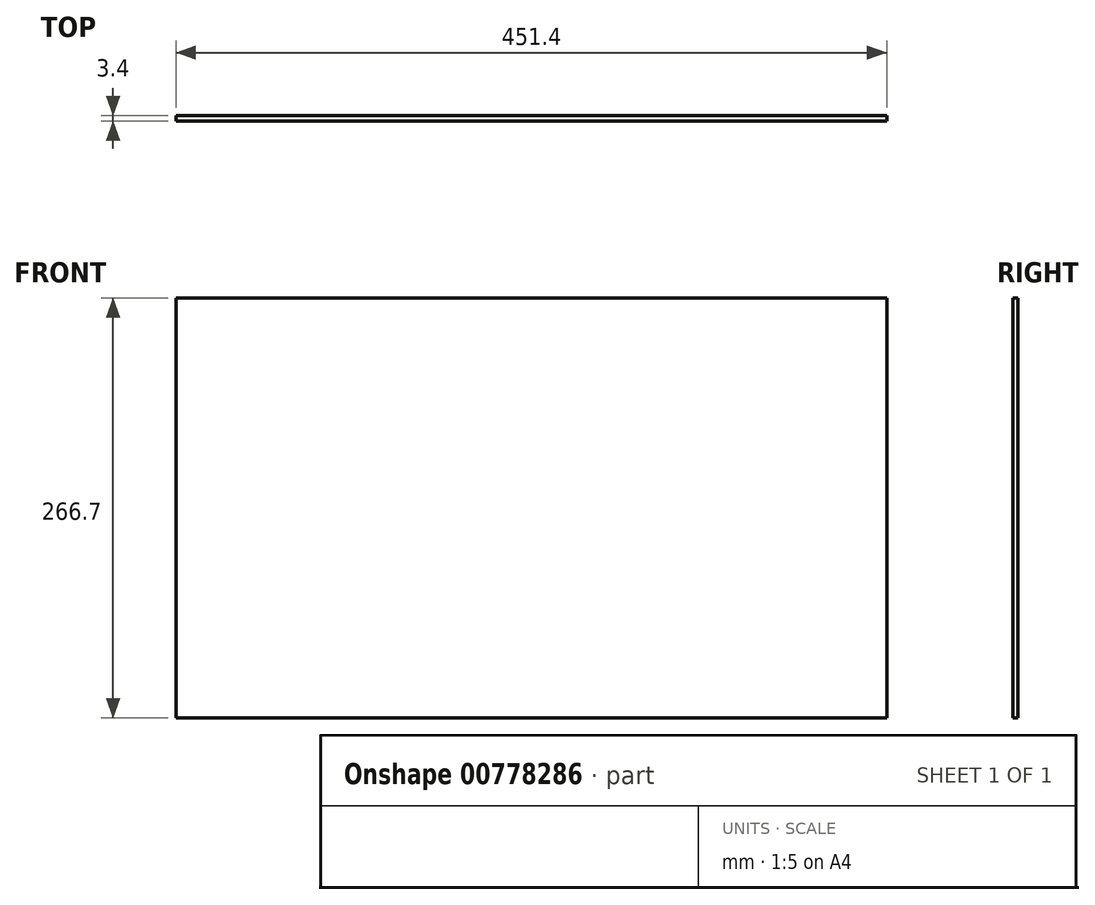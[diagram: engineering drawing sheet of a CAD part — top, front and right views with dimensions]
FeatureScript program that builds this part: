
annotation { "Feature Type Name" : "Feature", "Feature Type Description" : "" }
export const myFeature = defineFeature(function(context is Context, id is Id, definition is map)
    precondition{}
    {
        {
            var Q0;
            Q0=qCreatedBy(makeId("Front.planeOp"),FACE);
            var sketch = newSketch(context, id + "F0", { "sketchPlane" : qUnion([Q0])});
            skLineSegment(sketch, "E0.bottom", {"start": v(225.7, 133.35) * mm, "end": v(-225.7, 133.35) * mm});
            skLineSegment(sketch, "E0.top", {"start": v(225.7, -133.35) * mm, "end": v(-225.7, -133.35) * mm});
            skLineSegment(sketch, "E0.left", {"start": v(225.7, 133.35) * mm, "end": v(225.7, -133.35) * mm});
            skLineSegment(sketch, "E0.right", {"start": v(-225.7, 133.35) * mm, "end": v(-225.7, -133.35) * mm});
            skPoint(sketch, "E0.middle", {"position": v(0, 0) * mm});
            skSolve(sketch);
        }
        {
            var Q0;
            Q0=makeQuery(id+"F0.imprint","IMPRINT",FACE,{"disambiguationData":[TD([[makeQuery(id+"F0.imprint","IMPRINT",EDGE,{"derivedFrom":sQuery(id+"F0.wireOp",EDGE,"E0.bottom")}),1.0]])]});
            extrude(context, id + "F1", {"entities" : qUnion([Q0]), "depth" : 3.4 * mm, "offsetDistance" : 25.4 * mm});
        }
    });
